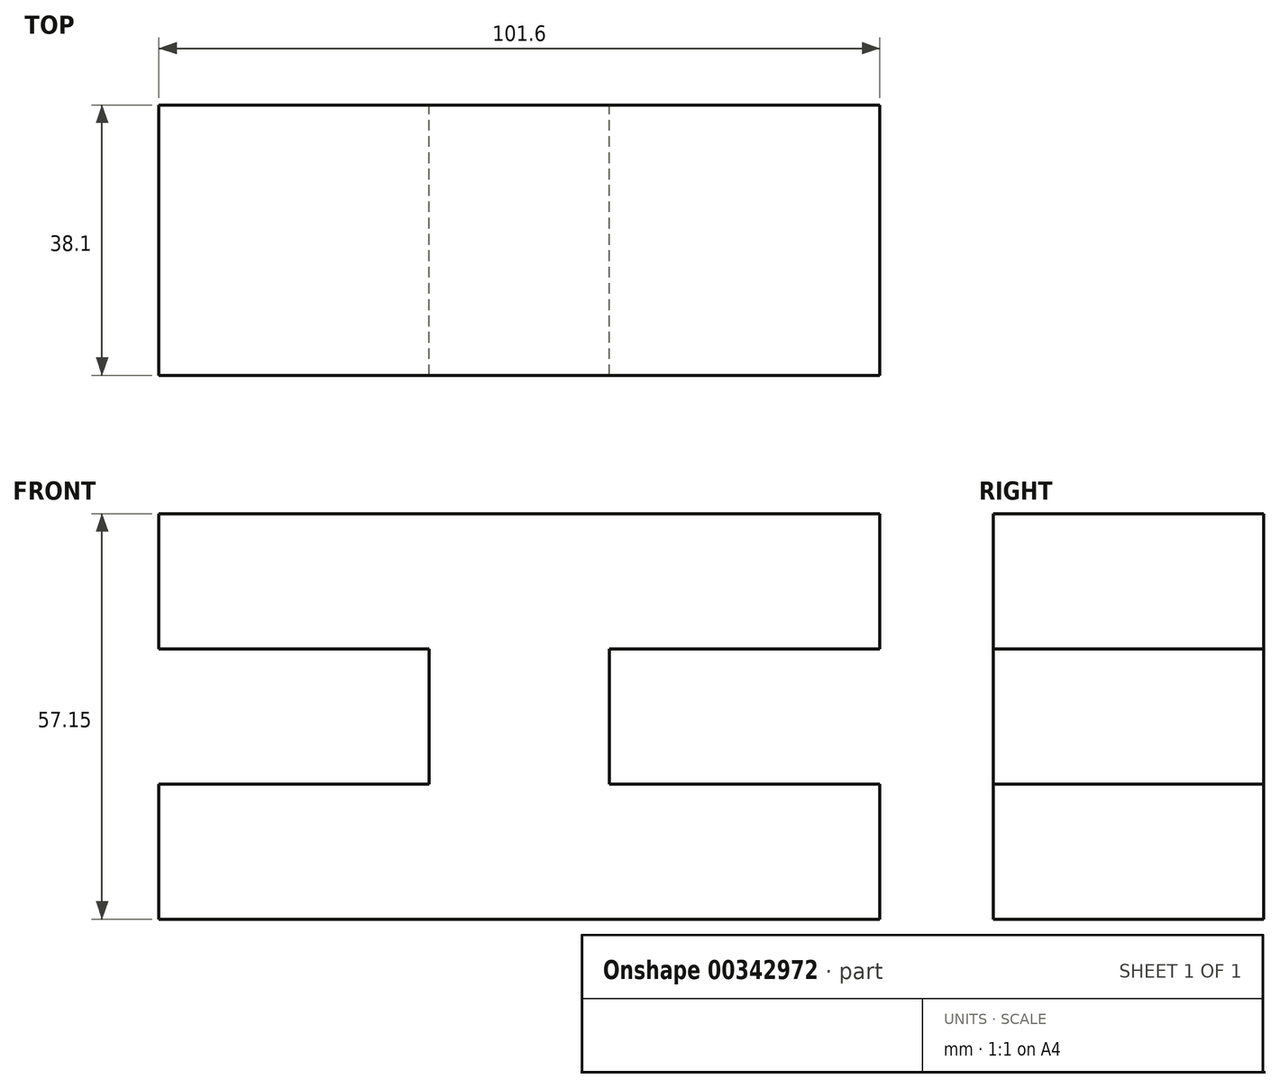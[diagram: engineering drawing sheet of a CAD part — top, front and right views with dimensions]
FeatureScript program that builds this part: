
annotation { "Feature Type Name" : "Feature", "Feature Type Description" : "" }
export const myFeature = defineFeature(function(context is Context, id is Id, definition is map)
    precondition{}
    {
        {
            var Q0;
            Q0=qCreatedBy(makeId("Front.planeOp"),FACE);
            var sketch = newSketch(context, id + "F0", { "sketchPlane" : qUnion([Q0])});
            skLineSegment(sketch, "E0", {"start": v(-38.1, 48.05) * mm, "end": v(63.5, 48.05) * mm});
            skLineSegment(sketch, "E1", {"start": v(63.5, 48.05) * mm, "end": v(63.5, 29) * mm});
            skLineSegment(sketch, "E2", {"start": v(63.5, 29) * mm, "end": v(25.4, 29) * mm});
            skLineSegment(sketch, "E3", {"start": v(25.4, 29) * mm, "end": v(25.4, 9.95) * mm});
            skLineSegment(sketch, "E4", {"start": v(25.4, 9.95) * mm, "end": v(63.5, 9.95) * mm});
            skLineSegment(sketch, "E5", {"start": v(63.5, 9.95) * mm, "end": v(63.5, -9.1) * mm});
            skLineSegment(sketch, "E6", {"start": v(63.5, -9.1) * mm, "end": v(-38.1, -9.1) * mm});
            skLineSegment(sketch, "E7", {"start": v(-38.1, -9.1) * mm, "end": v(-38.1, 9.95) * mm});
            skLineSegment(sketch, "E8", {"start": v(0, 29) * mm, "end": v(-38.1, 29) * mm});
            skLineSegment(sketch, "E9", {"start": v(-38.1, 29) * mm, "end": v(-38.1, 48.05) * mm});
            skLineSegment(sketch, "E10", {"start": v(-38.1, 9.95) * mm, "end": v(0, 9.95) * mm});
            skLineSegment(sketch, "E11", {"start": v(0, 29) * mm, "end": v(0, 9.95) * mm});
            skSolve(sketch);
        }
        {
            var Q0;
            Q0 = qSketchRegion(id + "F0", true);
            extrude(context, id + "F1", {"entities" : qUnion([Q0]), "depth" : 38.1 * mm});
        }
    });
